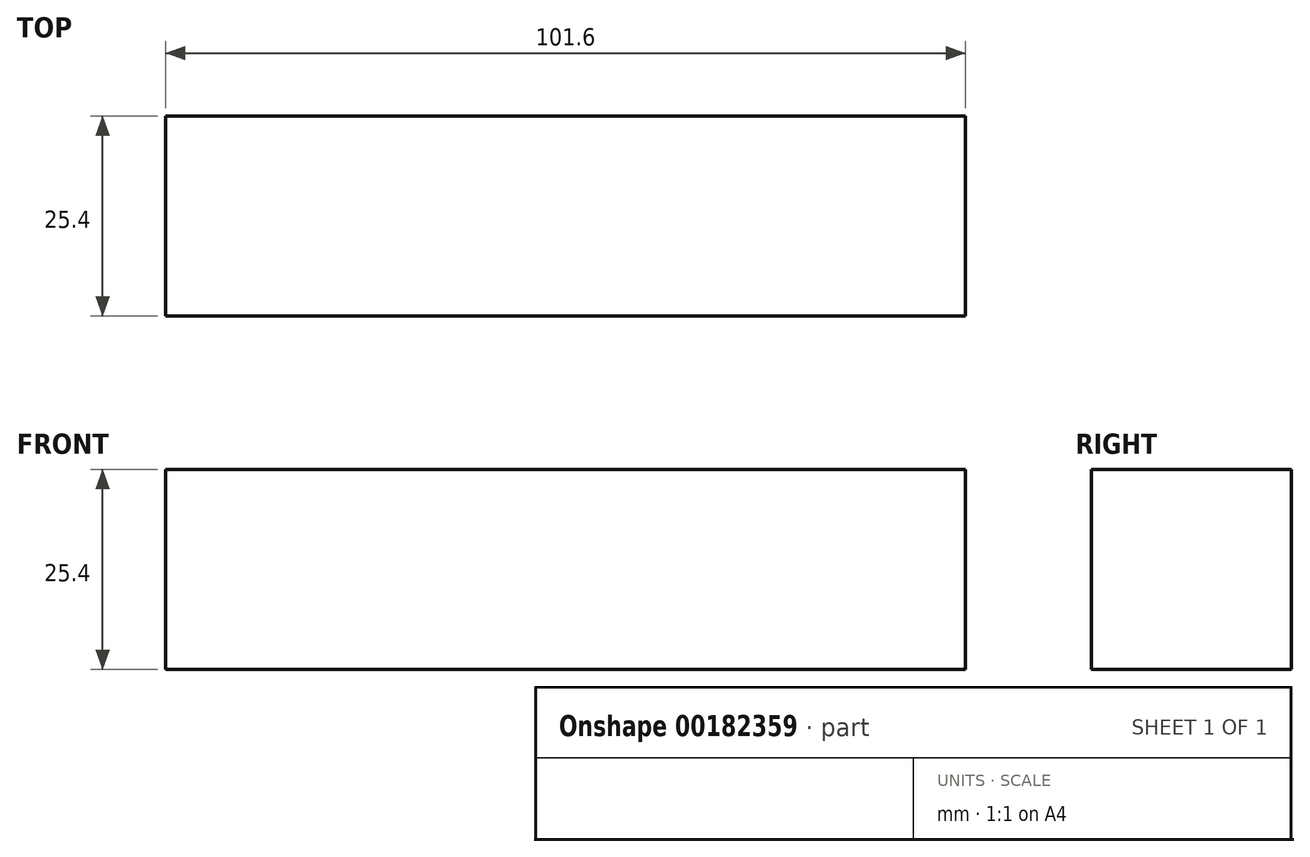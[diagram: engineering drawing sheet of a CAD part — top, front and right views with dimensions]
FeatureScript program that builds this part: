
annotation { "Feature Type Name" : "Feature", "Feature Type Description" : "" }
export const myFeature = defineFeature(function(context is Context, id is Id, definition is map)
    precondition{}
    {
        {
            var Q0;
            Q0=qCreatedBy(makeId("Top.planeOp"),FACE);
            var sketch = newSketch(context, id + "F0", { "sketchPlane" : qUnion([Q0])});
            skLineSegment(sketch, "E0.bottom", {"start": v(-29.28, -12.4) * mm, "end": v(72.32, -12.4) * mm});
            skLineSegment(sketch, "E0.top", {"start": v(-29.28, 13) * mm, "end": v(72.32, 13) * mm});
            skLineSegment(sketch, "E0.left", {"start": v(-29.28, -12.4) * mm, "end": v(-29.28, 13) * mm});
            skLineSegment(sketch, "E0.right", {"start": v(72.32, -12.4) * mm, "end": v(72.32, 13) * mm});
            skSolve(sketch);
        }
        {
            var Q0;
            Q0 = qSketchRegion(id + "F0", true);
            extrude(context, id + "F1", {"entities" : qUnion([Q0]), "depth" : 25.4 * mm});
        }
    });
